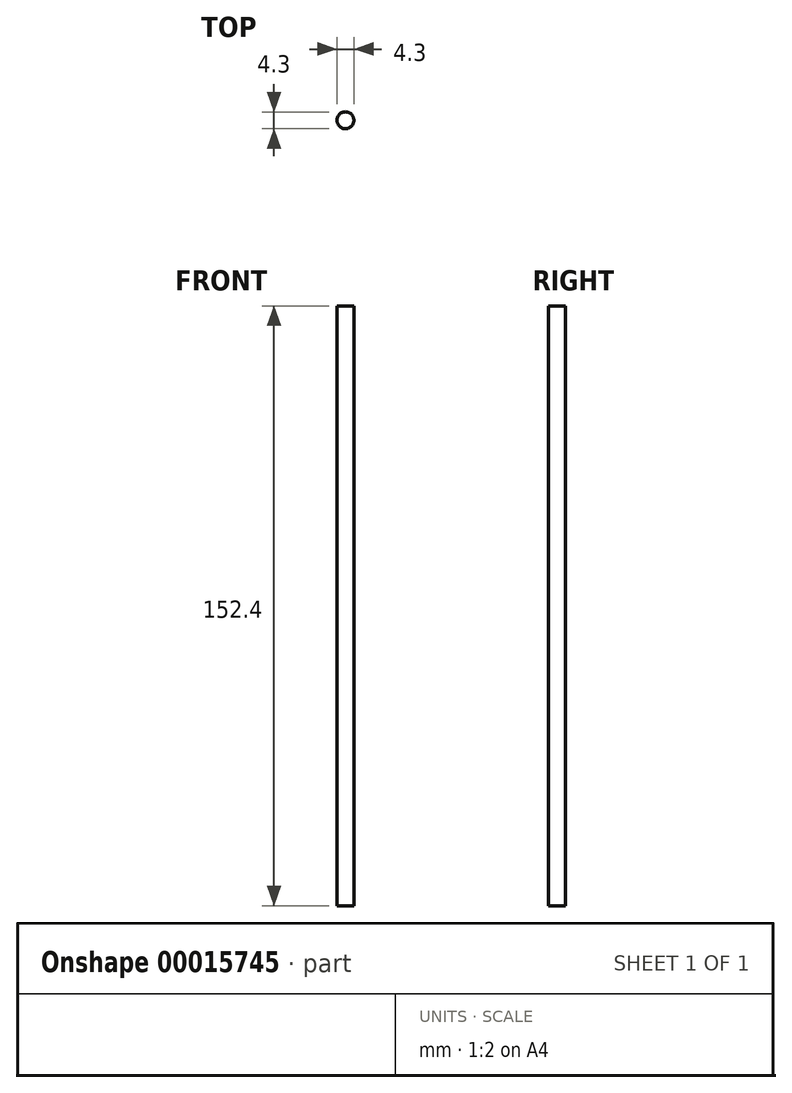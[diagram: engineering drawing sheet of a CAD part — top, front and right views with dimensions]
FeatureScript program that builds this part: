
annotation { "Feature Type Name" : "Feature", "Feature Type Description" : "" }
export const myFeature = defineFeature(function(context is Context, id is Id, definition is map)
    precondition{}
    {
        {
            var Q0;
            Q0=qCreatedBy(makeId("Top.planeOp"),FACE);
            var sketch = newSketch(context, id + "F0", { "sketchPlane" : qUnion([Q0])});
            skCircle(sketch, "E0", {"center": v(0, 0) * mm, "radius": 2.15 * mm});
            skSolve(sketch);
        }
        {
            var Q0;
            Q0 = qSketchRegion(id + "F0", true);
            extrude(context, id + "F1", {"entities" : qUnion([Q0]), "depth" : 152.4 * mm});
        }
    });
